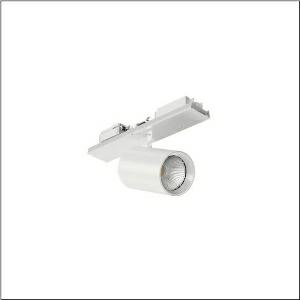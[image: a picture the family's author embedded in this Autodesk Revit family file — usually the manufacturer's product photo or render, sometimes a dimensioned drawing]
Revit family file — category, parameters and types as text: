
# Revit family: licross_r__spot_31_51sl14da45b_0bda
name_source: partatom
category: Lighting Fixtures
units: mm (PartAtom-declared; Revit-internal decimal feet)

## family parameters
Cut with Voids When Loaded = No
Host = Face
Light Source = No
Part Type = Normal
Room Calculation Point = No
Round Connector Dimension = Use Diameter
Shared = No

## types (1)
- --- (1 x LED, 5250 lm, 43.7 W, 4000K)
    Apparent Load = 44 VA
    CIE Flux Codes = 93 97 100 100 100
    Color Rendering = 90
    Color Temperature = 4000K
    Default Elevation = 1800 mm
    Description = Licross® Spot 31, directional spotlight, light control with lens, of plastic, LED rated luminous flux: 5.250lm, light colour: 940, with plug, 5-pole, mains connection: 220..240V, AC, 50/60Hz, of aluminium, traffic white (RAL 9016), length: 300mm, diameter: 90mm, protection rating (complete): IP20, insulation class (complete): insulation class I (protective earthing), certification: CE, packaging unit: 1 piece
    Height = 175 mm
    Lamp = 1 x LED
    Lamp Light Flux = 5250 lm
    Lamp Power = 43.7 W
    Lamp count = 1
    Length = 90 mm
    Luminous efficacy = 120 lm/W
    Manufacturer = Siteco
    ModVariant = No
    Model = 51SL14DA45B
    Mounting Place = Ceiling
    Mounting Type = Pendant
    Number of Poles = 1
    OnlyDefault = Yes
    Power Factor = 1
    Product Name = Licross® Spot 31
    Product group = directional spotlight
    ProductGroupID = 906
    Protection Class = Protection class I
    Protection Degree = IP 20
    RLX_Detail_Level = 1
    RLX_Emergency_Light_Flux = 0 lm
    RLX_Emergency_Type = 0
    RLX_Emergency_Type_DB = No
    RlxData = <blob elided: 14849 chars, md5=49e95d3a>
    Socket = socket
    Standby Power = 0 W
    System Light Flux = 5250 lm
    System Power = 44 W
    Type Comments = factory setting: luminous flux: 100 % | (ON | ON | ON) | 1050 mA
    Type Image = l_1245720.jpg
    URL = http://relux.com
    VarID = @adj_131752
    Voltage = 0 V
    Weight = 0.00 kg
    Width = 0 mm  [stored 0 ft]

note: [stored X ft] marks values corroborated as IEEE doubles in the binary element streams (Revit-internal decimal feet)

## geometry (parser evidence)
native form markers: Sweep x10
no freeform markers — native parametric forms only
